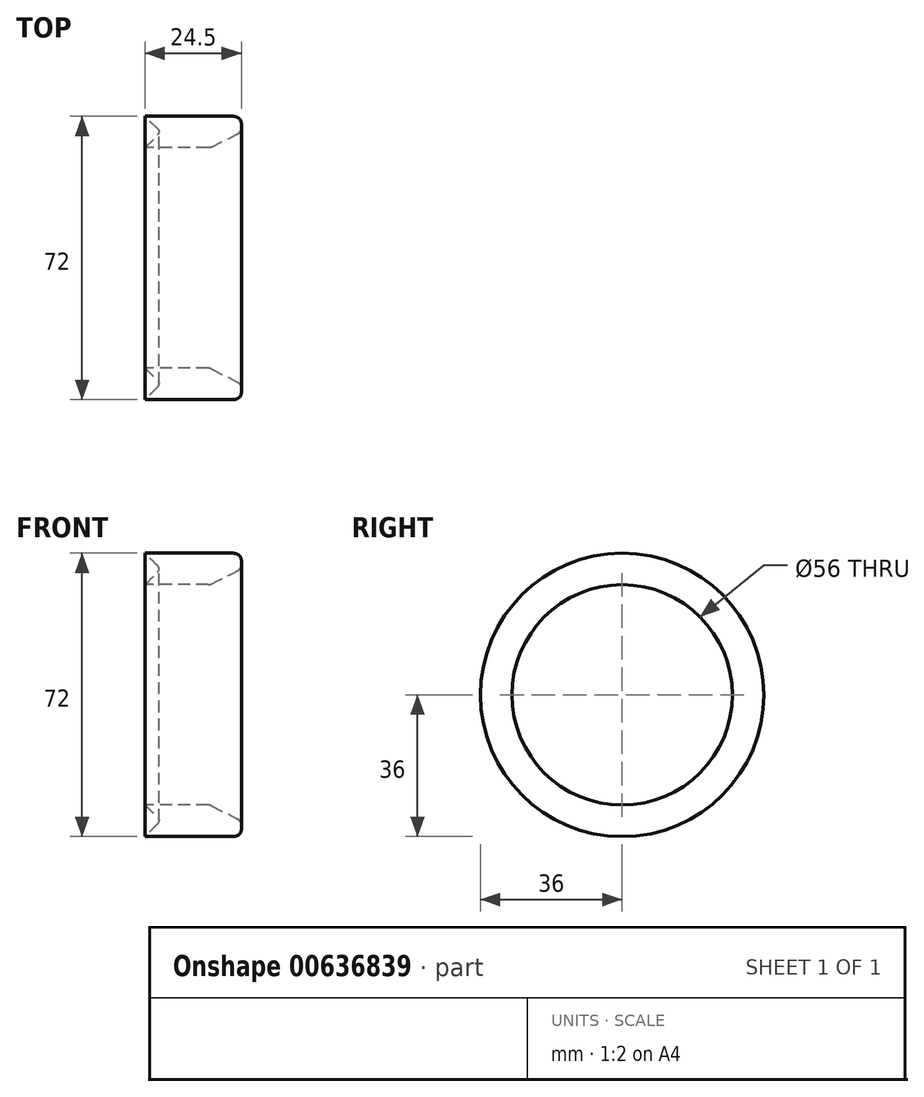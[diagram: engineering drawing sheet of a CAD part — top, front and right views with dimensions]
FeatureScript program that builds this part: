
annotation { "Feature Type Name" : "Feature", "Feature Type Description" : "" }
export const myFeature = defineFeature(function(context is Context, id is Id, definition is map)
    precondition{}
    {
        {
            var Q0;
            Q0=qCreatedBy(makeId("Right.planeOp"),FACE);
            var sketch = newSketch(context, id + "F0", { "sketchPlane" : qUnion([Q0])});
            skCircle(sketch, "E0", {"center": v(0, 0) * mm, "radius": 36 * mm});
            skCircle(sketch, "E1", {"center": v(0, 0) * mm, "radius": 28 * mm});
            skSolve(sketch);
        }
        {
            var Q0;
            Q0 = qSketchRegion(id + "F0", true);
            extrude(context, id + "F1", {"entities" : qUnion([Q0]), "depth" : 24.5 * mm, "offsetDistance" : 25 * mm});
        }
        {
            var Q0;
            Q0=makeQuery(id+"F1.opExtrude","CAP_FACE",FACE,{"disambiguationData":[OSD([sQuery(id+"F0.wireOp",EDGE,"E0"),sQuery(id+"F0.wireOp",EDGE,"E1")])],"isStart":true});
            var sketch = newSketch(context, id + "F2", { "sketchPlane" : qUnion([Q0])});
            skCircle(sketch, "E2.0", {"center": v(0, 0) * mm, "radius": 36 * mm});
            skCircle(sketch, "E3.0", {"center": v(0, 0) * mm, "radius": 28 * mm});
            skSolve(sketch);
        }
        {
            var Q0;
            Q0 = qSketchRegion(id + "F2", true);
            extrude(context, id + "F3", {"entities" : qUnion([Q0]), "depth" : 25 * mm, "offsetDistance" : 25 * mm});
        }
        {
            var Q0;
            Q0=makeQuery(id+"F3.opExtrude","CAP_EDGE",EDGE,{"disambiguationData":[OSD([sQuery(id+"F2.wireOp",EDGE,"E2.0")])],"isStart":true});
            var Q1;
            Q1=makeQuery(id+"F3.opExtrude","CAP_EDGE",EDGE,{"disambiguationData":[OSD([sQuery(id+"F2.wireOp",EDGE,"E3.0")])],"isStart":true});
            chamfer(context, id + "F4", {"entities" : qUnion([Q0, Q1]), "width" : 4 * mm, "tangentPropagation" : true});
        }
        {
            var Q0;
            Q0=makeQuery(id+"F4.opChamfer","BLEND_EDGE",EDGE,{"blendedFrom":[makeQuery(id+"F3.opExtrude","CAP_EDGE",EDGE,{"disambiguationData":[OSD([sQuery(id+"F2.wireOp",EDGE,"E2.0")])],"isStart":true}),makeQuery(id+"F3.opExtrude","CAP_EDGE",EDGE,{"disambiguationData":[OSD([sQuery(id+"F2.wireOp",EDGE,"E3.0")])],"isStart":true})],"blendedInto":[]});
            fillet(context, id + "F5", {"entities" : qUnion([Q0]), "radius" : 1 * mm, "tangentPropagation" : true, "allowEdgeOverflow" : false});
        }
        {
            var Q0;
            Q0=makeQuery(id+"F3.opExtrude","SWEPT_BODY",BODY,{"disambiguationData":[OSD([sQuery(id+"F2.wireOp",EDGE,"E2.0"),sQuery(id+"F2.wireOp",EDGE,"E3.0")])]});
            var Q1;
            {var subQ0=sQuery(id+"F2.wireOp",EDGE,"E2.0");Q1=makeQuery(id+"F4.opChamfer","BLEND_EDGE",EDGE,{"blendedFrom":[makeQuery(id+"F3.opExtrude","CAP_EDGE",EDGE,{"disambiguationData":[OSD([subQ0])],"isStart":true}),makeQuery(id+"F3.opExtrude","SWEPT_FACE",FACE,{"disambiguationData":[OSD([subQ0])]})],"blendedInto":[makeQuery(id+"F3.opExtrude","SWEPT_FACE",FACE,{"disambiguationData":[OSD([subQ0])]})]});}
            var Q2;
            Q2=makeQuery(id+"F1.opExtrude","SWEPT_FACE",FACE,{"disambiguationData":[OSD([sQuery(id+"F0.wireOp",EDGE,"E0")])]});
            transform(context, id + "F6", {"entities" : qUnion([Q0]), "transformType" : TransformType.TRANSLATION_DISTANCE, "transformDirection" : qUnion([Q2]), "distance" : 4 * mm, "oppositeDirection" : true, "makeCopy" : false});
        }
        {
            var Q0;
            Q0=makeQuery(id+"F3.opExtrude","SWEPT_BODY",BODY,{"disambiguationData":[OSD([sQuery(id+"F2.wireOp",EDGE,"E2.0"),sQuery(id+"F2.wireOp",EDGE,"E3.0")])]});
            var Q1;
            Q1=makeQuery(id+"F1.opExtrude","SWEPT_BODY",BODY,{"disambiguationData":[OSD([sQuery(id+"F0.wireOp",EDGE,"E0"),sQuery(id+"F0.wireOp",EDGE,"E1")])]});
            booleanBodies(context, id + "F7", {"operationType" : BooleanOperationType.SUBTRACTION, "tools" : qUnion([Q0]), "targets" : qUnion([Q1])});
        }
        {
            var Q0;
            Q0=makeQuery(id+"F1.opExtrude","CAP_EDGE",EDGE,{"disambiguationData":[OSD([sQuery(id+"F0.wireOp",EDGE,"E1")])],"isStart":false});
            chamfer(context, id + "F8", {"entities" : qUnion([Q0]), "chamferType" : ChamferType.TWO_OFFSETS, "width1" : 8 * mm, "oppositeDirection" : false, "width2" : 4 * mm, "tangentPropagation" : true});
        }
        {
            var Q0;
            {var subQ0=sQuery(id+"F0.wireOp",EDGE,"E1");Q0=makeQuery(id+"F8.opChamfer","BLEND_EDGE",EDGE,{"blendedFrom":[makeQuery(id+"F1.opExtrude","CAP_EDGE",EDGE,{"disambiguationData":[OSD([subQ0])],"isStart":false}),makeQuery(id+"F1.opExtrude","CAP_FACE",FACE,{"disambiguationData":[OSD([sQuery(id+"F0.wireOp",EDGE,"E0"),subQ0])],"isStart":false})],"blendedInto":[makeQuery(id+"F1.opExtrude","CAP_FACE",FACE,{"disambiguationData":[OSD([sQuery(id+"F0.wireOp",EDGE,"E0"),subQ0])],"isStart":false})]});}
            var Q1;
            Q1=makeQuery(id+"F1.opExtrude","CAP_EDGE",EDGE,{"disambiguationData":[OSD([sQuery(id+"F0.wireOp",EDGE,"E0")])],"isStart":false});
            fillet(context, id + "F9", {"entities" : qUnion([Q0, Q1]), "radius" : 2 * mm, "tangentPropagation" : true, "allowEdgeOverflow" : false});
        }
        {
            var Q0;
            {var subQ0=sQuery(id+"F0.wireOp",EDGE,"E1");Q0=makeQuery(id+"F8.opChamfer","BLEND_EDGE",EDGE,{"blendedFrom":[makeQuery(id+"F1.opExtrude","CAP_EDGE",EDGE,{"disambiguationData":[OSD([subQ0])],"isStart":false}),makeQuery(id+"F1.opExtrude","SWEPT_FACE",FACE,{"disambiguationData":[OSD([subQ0])]})],"blendedInto":[makeQuery(id+"F1.opExtrude","SWEPT_FACE",FACE,{"disambiguationData":[OSD([subQ0])]})]});}
            fillet(context, id + "F10", {"entities" : qUnion([Q0]), "radius" : 2 * mm, "tangentPropagation" : true, "allowEdgeOverflow" : false});
        }
    });
